# Revit family: NLRS_57_DUF_UN_rechthoekig-radius-T-stuk-inline_nijburg
name_source: partatom
category: Duct Fittings
units: mm (PartAtom-declared; Revit-internal decimal feet)

## family parameters
Always vertical = Yes
Cut with Voids When Loaded = No
Part Type = Tee
Round Connector Dimension = Use Diameter
Shared = No
Work Plane-Based = No

## types (4) — shared parameters
Assembly Code = 57.70
Description = Rechthoekig Radius T-stuk inline
Manufacturer = Nijburg Klimaattechniek BV
Model = T-stuk inlne
NLRS_C_content_datum_gewijzigd = 05-05-2023
NLRS_C_content_provider = Nijburg Klimaattechniek BV
NLRS_C_content_versie = 1.20.00
NLRS_C_description = Rechthoekig Radius T-stuk inline
NLRS_C_model = T-stuk inlne
NPR_Artikelcode = RHKV
URL = https://nijburg-klimaattechniek.nl
zero-valued in all types: Default Elevation

## per-type parameters (varying)
| type | NPR_Radius |
| R=170 (std) | 170 mm  [stored 0.557743 ft] |
| R=100 | 100 mm  [stored 0.328084 ft] |
| R=120 | 120 mm  [stored 0.393701 ft] |
| R=150 | 150 mm |

note: [stored X ft] marks values corroborated as IEEE doubles in the binary element streams (Revit-internal decimal feet)

## geometry (parser evidence)
native form markers: Sweep x5
no freeform markers — native parametric forms only
